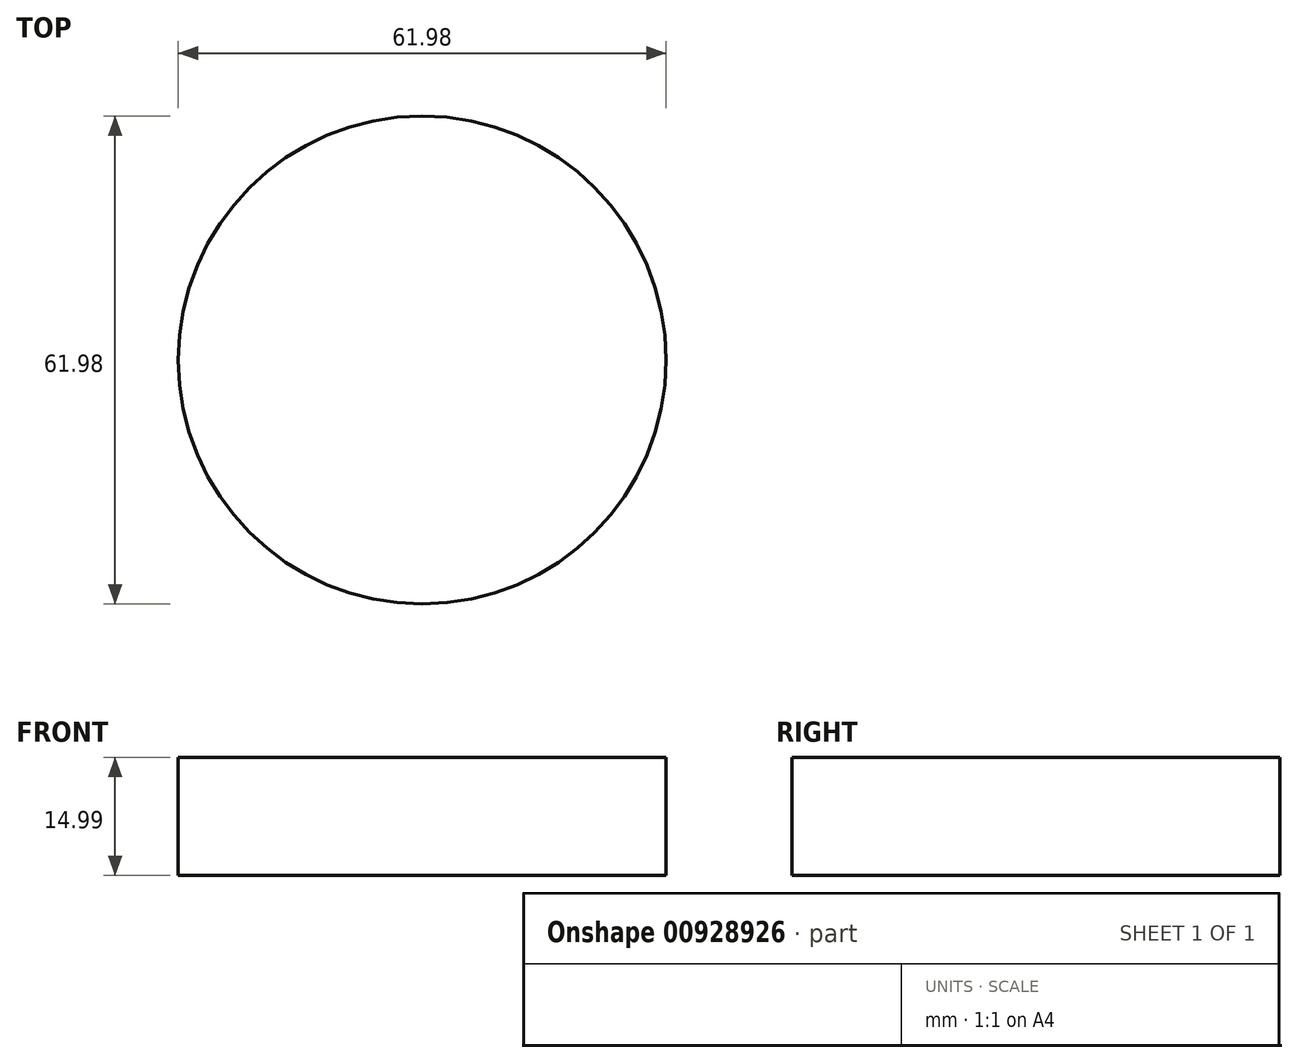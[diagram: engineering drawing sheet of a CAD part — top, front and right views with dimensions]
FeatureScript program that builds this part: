
annotation { "Feature Type Name" : "Feature", "Feature Type Description" : "" }
export const myFeature = defineFeature(function(context is Context, id is Id, definition is map)
    precondition{}
    {
        {
            var Q0;
            Q0=qCreatedBy(makeId("Top.planeOp"),FACE);
            var sketch = newSketch(context, id + "F0", { "sketchPlane" : qUnion([Q0])});
            skCircle(sketch, "E0", {"center": v(0, 0) * mm, "radius": 30.99 * mm});
            skSolve(sketch);
        }
        {
            var Q0;
            Q0 = qSketchRegion(id + "F0", true);
            extrude(context, id + "F1", {"entities" : qUnion([Q0]), "depth" : 15 * mm, "offsetDistance" : 25.4 * mm});
        }
    });
